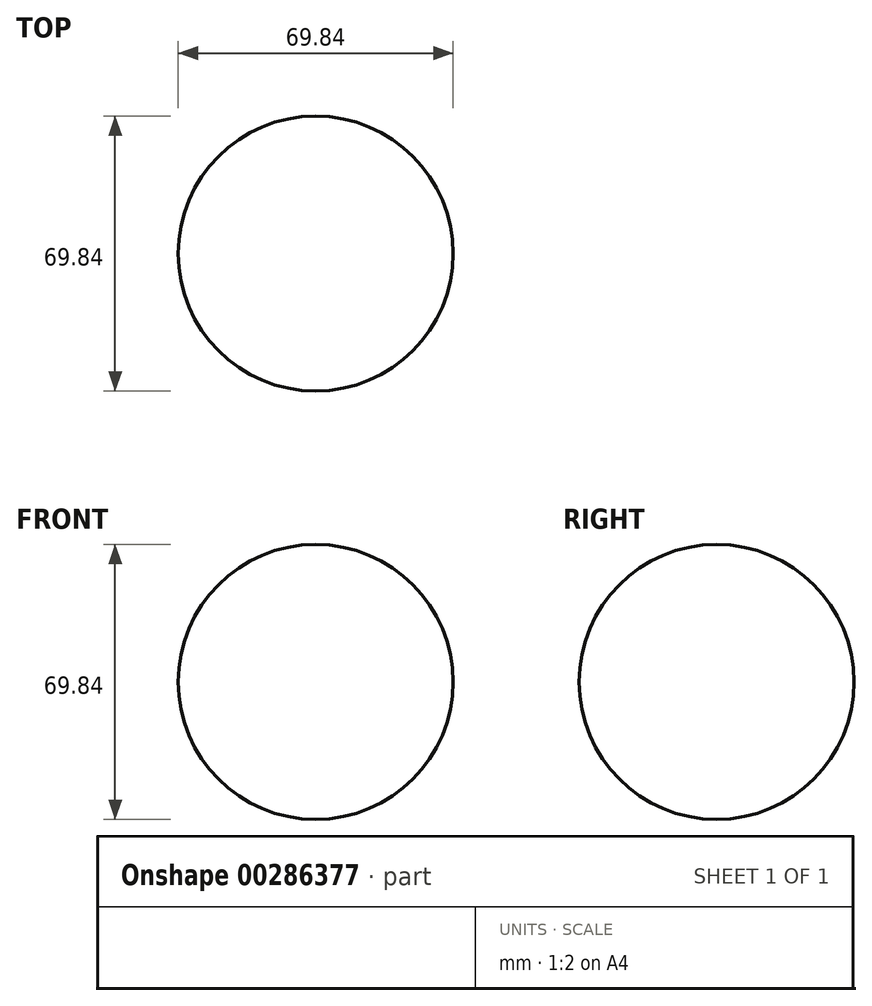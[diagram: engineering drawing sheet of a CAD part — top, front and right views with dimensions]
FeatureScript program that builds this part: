
annotation { "Feature Type Name" : "Feature", "Feature Type Description" : "" }
export const myFeature = defineFeature(function(context is Context, id is Id, definition is map)
    precondition{}
    {
        {
            var Q0;
            Q0=qCreatedBy(makeId("Right.planeOp"),FACE);
            var sketch = newSketch(context, id + "F0", { "sketchPlane" : qUnion([Q0])});
            skArc(sketch, "E0", {"start": v(0, 34.93) * mm, "mid": v(-34.93, 0) * mm, "end": v(0, -34.93) * mm});
            skLineSegment(sketch, "E1", {"start": v(0, -57.78) * mm, "end": v(0, 71.26) * mm, "construction": true});
            skLineSegment(sketch, "E2", {"start": v(0, 34.93) * mm, "end": v(0, -34.93) * mm});
            skSolve(sketch);
        }
        {
            var Q0;
            Q0=makeQuery(id+"F0.imprint","IMPRINT",FACE,{"disambiguationData":[TD([[makeQuery(id+"F0.imprint","IMPRINT",EDGE,{"derivedFrom":sQuery(id+"F0.wireOp",EDGE,"E0")}),1.0]])]});
            var Q1;
            Q1=sQuery(id+"F0.wireOp",EDGE,"E0");
            var Q2;
            Q2=sQuery(id+"F0.wireOp",EDGE,"E1");
            revolve(context, id + "F1", {"entities" : qUnion([Q0]), "surfaceEntities" : qUnion([Q1]), "axis" : qUnion([Q2]), "revolveType" : RevolveType.FULL});
        }
    });
